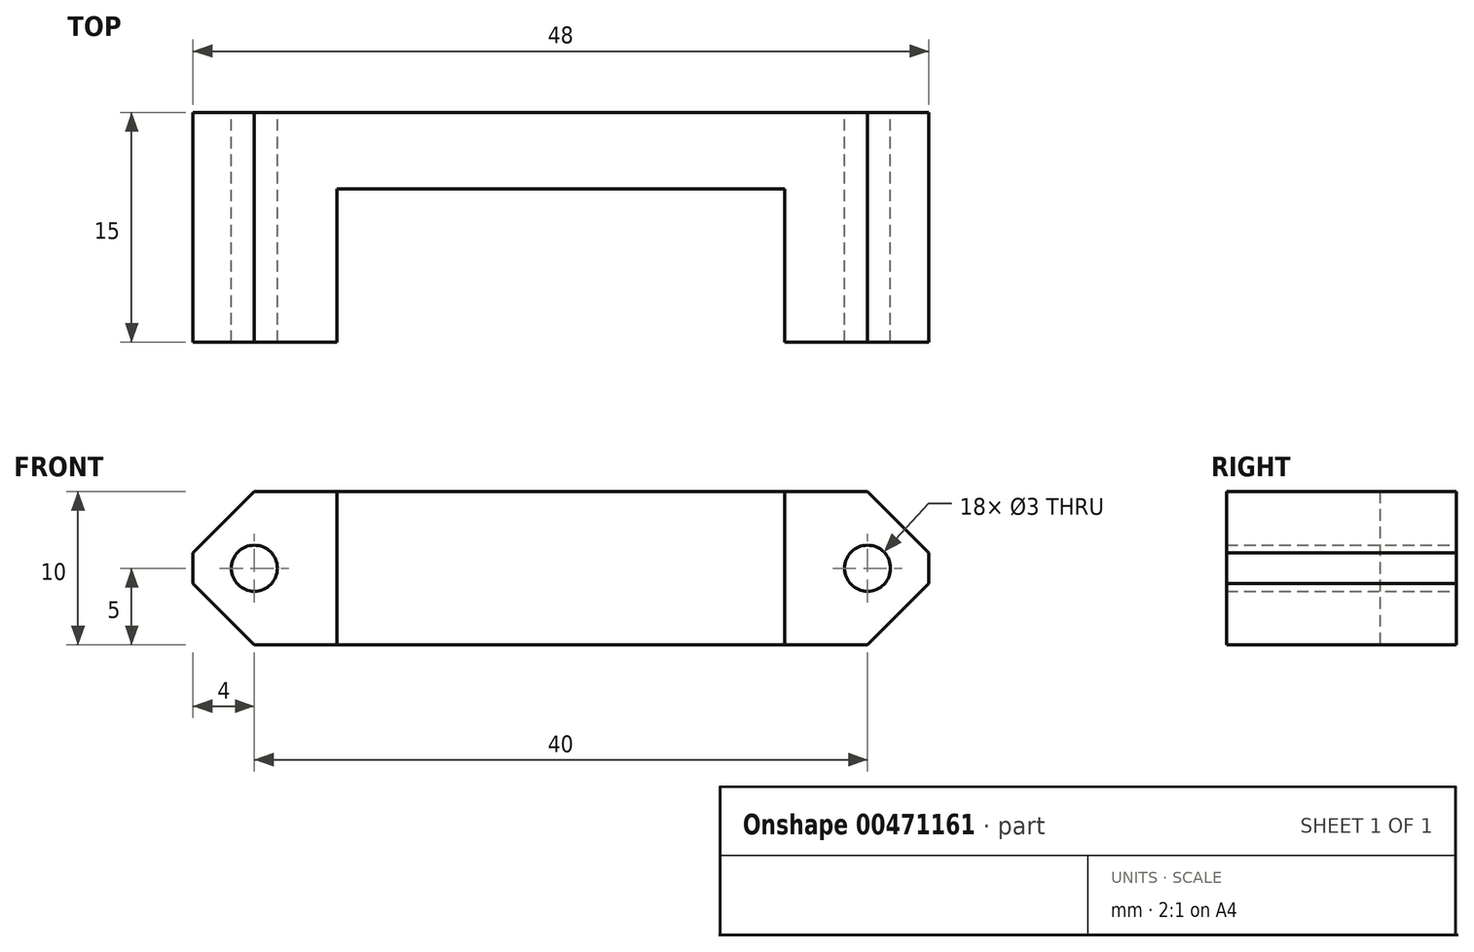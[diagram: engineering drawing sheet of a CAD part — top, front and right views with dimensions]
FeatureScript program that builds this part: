
annotation { "Feature Type Name" : "Feature", "Feature Type Description" : "" }
export const myFeature = defineFeature(function(context is Context, id is Id, definition is map)
    precondition{}
    {
        {
            var Q0;
            Q0=qCreatedBy(makeId("Front.planeOp"),FACE);
            var sketch = newSketch(context, id + "F0", { "sketchPlane" : qUnion([Q0])});
            skLineSegment(sketch, "E0", {"start": v(20, 0) * mm, "end": v(24, 4) * mm});
            skLineSegment(sketch, "E1", {"start": v(24, 4) * mm, "end": v(24, 6) * mm});
            skLineSegment(sketch, "E2", {"start": v(24, 6) * mm, "end": v(20, 10) * mm});
            skLineSegment(sketch, "E3", {"start": v(20, 0) * mm, "end": v(0, 0) * mm});
            skLineSegment(sketch, "E4", {"start": v(0, 10) * mm, "end": v(20, 10) * mm});
            skLineSegment(sketch, "E5.MirrorCS", {"start": v(0, 10) * mm, "end": v(-20, 10) * mm});
            skLineSegment(sketch, "E6.MirrorCS", {"start": v(-24, 6) * mm, "end": v(-20, 10) * mm});
            skLineSegment(sketch, "E7.MirrorCS", {"start": v(-24, 4) * mm, "end": v(-24, 6) * mm});
            skLineSegment(sketch, "E8.MirrorCS", {"start": v(-20, 0) * mm, "end": v(-24, 4) * mm});
            skLineSegment(sketch, "E9.MirrorCS", {"start": v(-20, 0) * mm, "end": v(0, 0) * mm});
            skCircle(sketch, "E10", {"center": v(20, 5) * mm, "radius": 1.5 * mm});
            skCircle(sketch, "E11.MirrorC", {"center": v(-20, 5) * mm, "radius": 1.5 * mm});
            skSolve(sketch);
        }
        {
            var Q0;
            Q0=makeQuery(id+"F0.imprint","IMPRINT",FACE,{"disambiguationData":[TD([[makeQuery(id+"F0.imprint","IMPRINT",EDGE,{"derivedFrom":sQuery(id+"F0.wireOp",EDGE,"E0")}),1.0]])]});
            extrude(context, id + "F1", {"entities" : qUnion([Q0]), "depth" : 15 * mm});
        }
        {
            var Q0;
            Q0=qCreatedBy(makeId("Top.planeOp"),FACE);
            var sketch = newSketch(context, id + "F2", { "sketchPlane" : qUnion([Q0])});
            skLineSegment(sketch, "E12.bottom", {"start": v(-14.6, -15) * mm, "end": v(14.6, -15) * mm});
            skLineSegment(sketch, "E12.top", {"start": v(-14.6, -5) * mm, "end": v(14.6, -5) * mm});
            skLineSegment(sketch, "E12.left", {"start": v(-14.6, -15) * mm, "end": v(-14.6, -5) * mm});
            skLineSegment(sketch, "E12.right", {"start": v(14.6, -15) * mm, "end": v(14.6, -5) * mm});
            skSolve(sketch);
        }
        {
            var Q0;
            Q0 = qSketchRegion(id + "F2", true);
            extrude(context, id + "F3", {"entities" : qUnion([Q0]), "operationType" : NewBodyOperationType.REMOVE, "endBound" : BoundingType.THROUGH_ALL, "depth" : 25 * mm});
        }
    });
